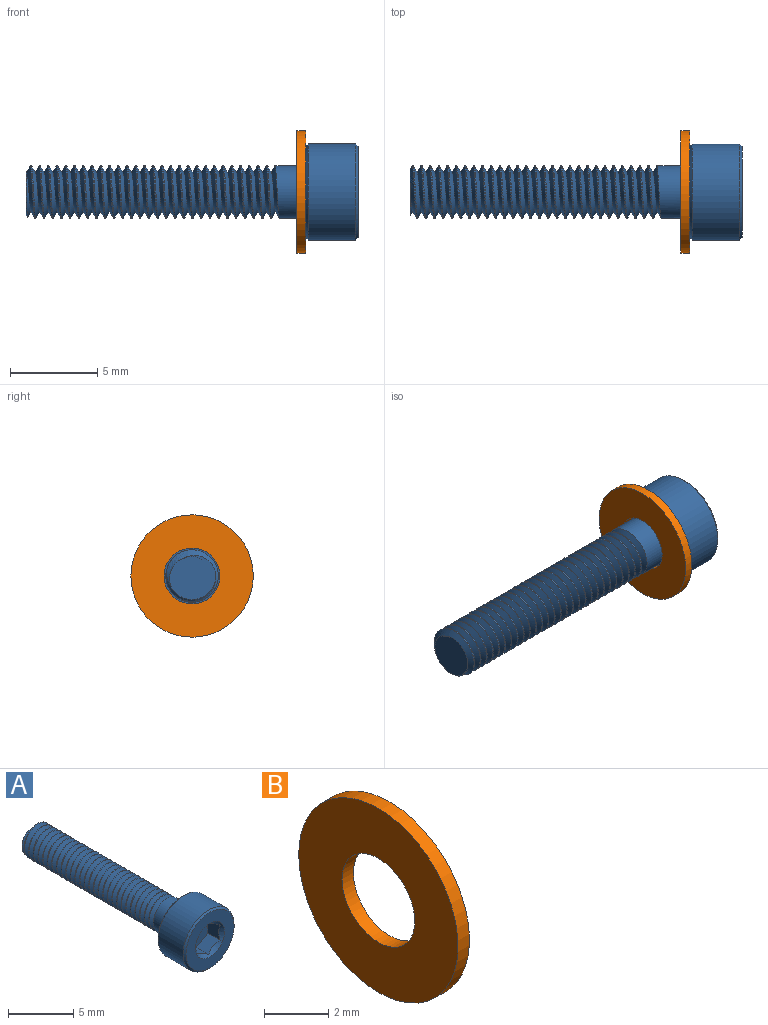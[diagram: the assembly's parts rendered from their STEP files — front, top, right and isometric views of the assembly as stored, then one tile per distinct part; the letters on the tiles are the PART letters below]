
ASSEMBLY  parts=2 mates=1
PART A: 49 faces, bbox 5.6x19.4x5.6 mm
  f0: cylinder r=1.5mm len=3mm, axis (0,1,0), area 16.3mm2, adj f1,f31,f34,f46,f47,f48
  f1: cylinder r=1.5mm len=3mm, axis (0,1,0), area 0.6mm2, adj f0,f2,f47,f48
  f2: cylinder r=1.5mm len=3mm, axis (0,1,0), area 0.6mm2, adj f1,f3,f47,f48
  f3: cylinder r=1.5mm len=3mm, axis (0,1,0), area 0.6mm2, adj f2,f4,f47,f48
  f4: cylinder r=1.5mm len=3mm, axis (0,1,0), area 0.6mm2, adj f3,f5,f47,f48
  f5: cylinder r=1.5mm len=3mm, axis (0,1,0), area 0.6mm2, adj f4,f6,f47,f48
  f6: cylinder r=1.5mm len=3mm, axis (0,1,0), area 0.6mm2, adj f5,f7,f47,f48
  f7: cylinder r=1.5mm len=3mm, axis (0,1,0), area 0.6mm2, adj f6,f8,f47,f48
  f8: cylinder r=1.5mm len=3mm, axis (0,1,0), area 0.6mm2, adj f7,f9,f47,f48
  f9: cylinder r=1.5mm len=3mm, axis (0,1,0), area 0.6mm2, adj f8,f10,f47,f48
  f10: cylinder r=1.5mm len=3mm, axis (0,1,0), area 0.6mm2, adj f9,f11,f47,f48
  f11: cylinder r=1.5mm len=3mm, axis (0,1,0), area 0.6mm2, adj f10,f12,f47,f48
  f12: cylinder r=1.5mm len=3mm, axis (0,1,0), area 0.6mm2, adj f11,f13,f47,f48
  f13: cylinder r=1.5mm len=3mm, axis (0,1,0), area 0.6mm2, adj f12,f14,f47,f48
  f14: cylinder r=1.5mm len=3mm, axis (0,1,0), area 0.6mm2, adj f13,f15,f47,f48
  f15: cylinder r=1.5mm len=3mm, axis (0,1,0), area 0.6mm2, adj f14,f16,f47,f48
  f16: cylinder r=1.5mm len=3mm, axis (0,1,0), area 0.6mm2, adj f15,f17,f47,f48
  f17: cylinder r=1.5mm len=3mm, axis (0,1,0), area 0.6mm2, adj f16,f18,f47,f48
  f18: cylinder r=1.5mm len=3mm, axis (0,1,0), area 0.6mm2, adj f17,f19,f47,f48
  f19: cylinder r=1.5mm len=3mm, axis (0,1,0), area 0.6mm2, adj f18,f20,f47,f48
  f20: cylinder r=1.5mm len=3mm, axis (0,1,0), area 0.6mm2, adj f19,f21,f47,f48
  f21: cylinder r=1.5mm len=3mm, axis (0,1,0), area 0.6mm2, adj f20,f22,f47,f48
  f22: cylinder r=1.5mm len=3mm, axis (0,1,0), area 0.6mm2, adj f21,f23,f47,f48
  f23: cylinder r=1.5mm len=3mm, axis (0,1,0), area 0.6mm2, adj f22,f24,f47,f48
  f24: cylinder r=1.5mm len=3mm, axis (0,1,0), area 0.6mm2, adj f23,f25,f47,f48
  f25: cylinder r=1.5mm len=3mm, axis (0,1,0), area 0.6mm2, adj f24,f26,f47,f48
  f26: cylinder r=1.5mm len=3mm, axis (0,1,0), area 0.6mm2, adj f25,f27,f47,f48
  f27: cylinder r=1.5mm len=3mm, axis (0,1,0), area 0.6mm2, adj f26,f28,f47,f48
  f28: cylinder r=1.5mm len=3mm, axis (0,1,0), area 0.3mm2, adj f27,f30,f47,f48
  f29: plane 2.75x2.64mm, normal (0,1,0), area 5.2mm2, adj f30,f47,f48
  f30: cone r=1.35mm half-angle=45deg, axis (0,-1,0), area 0.5mm2, adj f28,f29,f47,f48
  f31: plane 1x0.38mm, normal (0,-0.87,-0.5), area 0.3mm2, adj f0,f46,f47
  f32: cylinder r=2.75mm len=5.5mm, axis (0,1,0), area 46.7mm2, adj f44,f45
  f33: plane 5.2x5.2mm, normal (0,-1,0), area 13.5mm2, adj f35,f45
  f34: plane 5.2x5.2mm, normal (0,1,0), area 14.2mm2, adj f0,f44
  f35: cone r=1.57mm half-angle=45deg, axis (0,-1,0), area 3.2mm2, adj f33,f37,f38,f39,f40,f41,f42
  f36: plane 2.89x2.5mm, normal (0,-1,0), area 5.4mm2, adj f37,f38,f39,f40,f41,f42,f43
  f37: plane 1.59x1.52mm, normal (-1,0,0), area 1.8mm2, adj f35,f36,f38,f42
  f38: plane 1.38x1.25mm, normal (-0.5,0,0.87), area 1.8mm2, adj f35,f36,f37,f39
  f39: plane 1.38x1.25mm, normal (0.5,0,0.87), area 1.8mm2, adj f35,f36,f38,f40
  f40: plane 1.45x1.38mm, normal (1,0,0), area 1.8mm2, adj f35,f36,f39,f41
  f41: plane 1.38x1.25mm, normal (0.5,0,-0.87), area 1.8mm2, adj f35,f36,f40,f42
  f42: plane 1.38x1.25mm, normal (-0.5,0,-0.87), area 1.8mm2, adj f35,f36,f37,f41
  f43: cone r=1.57mm half-angle=45deg, axis (0,-1,0), area 0mm2, adj f36
  f44: cone r=2.6mm half-angle=45deg, axis (0,-1,0), area 3.6mm2, adj f32,f34
  f45: cone r=2.75mm half-angle=45deg, axis (0,1,0), area 3.6mm2, adj f32,f33
  f46: plane 1.28x0.4mm, normal (0,0.87,-0.5), area 0.4mm2, adj f0,f31,f48
  f47: bspline ~14.55x3.46mm, area 102.6mm2, adj f0,f1,f2,f3,f4,f5,f6,f7
  f48: bspline ~14.64x3.46mm, area 104mm2, adj f0,f1,f2,f3,f4,f5,f6,f7
PART B: 4 faces, bbox 0.5x7x7 mm
  f0: plane 7x7mm, normal (-1,0,0), area 30.4mm2, adj f1,f3
  f1: cylinder r=1.6mm len=3.2mm, axis (1,0,0), area 5mm2, adj f0,f2
  f2: plane 7x7mm, normal (1,0,0), area 30.4mm2, adj f1,f3
  f3: cylinder r=3.5mm len=7mm, axis (1,0,0), area 11mm2, adj f0,f2
PLACE A rot(axis=(0,0,1),90deg) t=(-15.5,0,0)mm
PLACE B at identity fixed
MATE fastened A.f0 <-> B.f1  axis (1,0,0) through (0.5,0,0)mm
